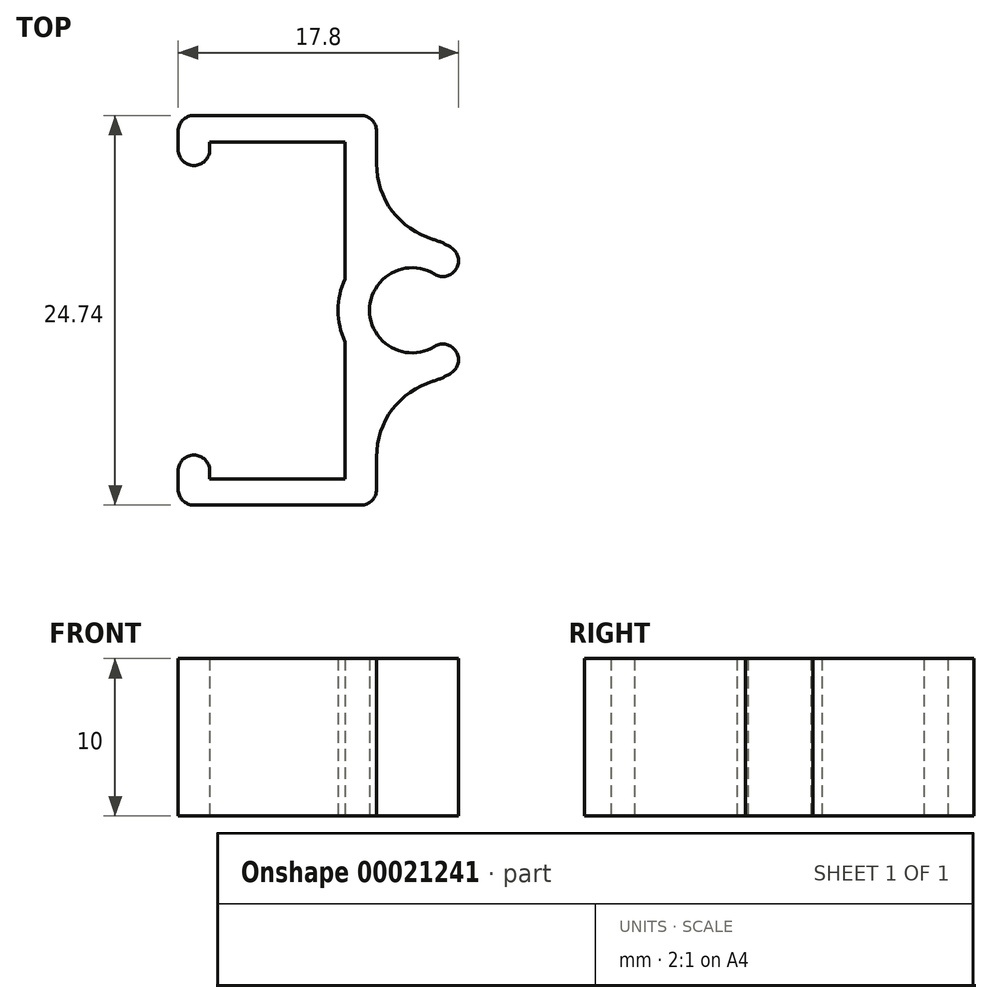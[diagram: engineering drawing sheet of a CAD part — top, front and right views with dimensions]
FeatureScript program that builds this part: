
annotation { "Feature Type Name" : "Feature", "Feature Type Description" : "" }
export const myFeature = defineFeature(function(context is Context, id is Id, definition is map)
    precondition{}
    {
        {
            var Q0;
            Q0=qCreatedBy(makeId("Top.planeOp"),FACE);
            var sketch = newSketch(context, id + "F0", { "sketchPlane" : qUnion([Q0])});
            skLineSegment(sketch, "E0", {"start": v(0.45, 10.7) * mm, "end": v(-8.15, 10.7) * mm});
            skLineSegment(sketch, "E1", {"start": v(-8.15, 10.7) * mm, "end": v(-8.15, 10.2) * mm});
            skLineSegment(sketch, "E2", {"start": v(-9.15, 9.2) * mm, "end": v(-9.15, 9.2) * mm});
            skLineSegment(sketch, "E3", {"start": v(-10.15, 10.2) * mm, "end": v(-10.15, 11.37) * mm});
            skLineSegment(sketch, "E4", {"start": v(-9.15, 12.37) * mm, "end": v(1.45, 12.37) * mm});
            skLineSegment(sketch, "E5.MirrorCS", {"start": v(-8.15, -10.7) * mm, "end": v(-8.15, -10.2) * mm});
            skLineSegment(sketch, "E6.MirrorCS", {"start": v(-9.15, -9.2) * mm, "end": v(-9.15, -9.2) * mm});
            skLineSegment(sketch, "E7.MirrorCS", {"start": v(-10.15, -10.2) * mm, "end": v(-10.15, -11.37) * mm});
            skLineSegment(sketch, "E8.MirrorCS", {"start": v(0.45, -10.7) * mm, "end": v(-8.15, -10.7) * mm});
            skLineSegment(sketch, "E9", {"start": v(2.45, 11.37) * mm, "end": v(2.45, 4.12) * mm});
            skLineSegment(sketch, "E10.MirrorCS", {"start": v(-9.15, -12.37) * mm, "end": v(1.45, -12.37) * mm});
            skLineSegment(sketch, "E11.MirrorCS", {"start": v(2.45, -11.37) * mm, "end": v(2.45, -4.12) * mm});
            skLineSegment(sketch, "E12", {"start": v(0.45, 10.7) * mm, "end": v(0.45, 2) * mm});
            skLineSegment(sketch, "E13.MirrorCS", {"start": v(0.45, -10.7) * mm, "end": v(0.45, -2) * mm});
            skArc(sketch, "E14", {"start": v(7.18, 4) * mm, "mid": v(0, 0) * mm, "end": v(7.18, -4) * mm});
            skPoint(sketch, "E15.visualSharp", {"position": v(2.45, 12.37) * mm});
            skArc(sketch, "E15.filletArc", {"start": v(2.45, 11.37) * mm, "mid": v(2.15, 12.08) * mm, "end": v(1.45, 12.37) * mm});
            skPoint(sketch, "E16.visualSharp", {"position": v(2.45, -12.37) * mm});
            skArc(sketch, "E16.filletArc", {"start": v(1.45, -12.37) * mm, "mid": v(2.15, -12.08) * mm, "end": v(2.45, -11.37) * mm});
            skPoint(sketch, "E17.visualSharp", {"position": v(-10.15, -12.37) * mm});
            skArc(sketch, "E17.filletArc", {"start": v(-10.15, -11.37) * mm, "mid": v(-9.86, -12.08) * mm, "end": v(-9.15, -12.37) * mm});
            skPoint(sketch, "E18.visualSharp", {"position": v(-10.15, -9.2) * mm});
            skArc(sketch, "E18.filletArc", {"start": v(-9.15, -9.2) * mm, "mid": v(-9.86, -9.5) * mm, "end": v(-10.15, -10.2) * mm});
            skPoint(sketch, "E19.visualSharp", {"position": v(-8.15, -9.2) * mm});
            skArc(sketch, "E19.filletArc", {"start": v(-8.15, -10.2) * mm, "mid": v(-8.45, -9.5) * mm, "end": v(-9.15, -9.2) * mm});
            skPoint(sketch, "E20.visualSharp", {"position": v(-8.15, 9.2) * mm});
            skArc(sketch, "E20.filletArc", {"start": v(-9.15, 9.2) * mm, "mid": v(-8.45, 9.5) * mm, "end": v(-8.15, 10.2) * mm});
            skPoint(sketch, "E21.visualSharp", {"position": v(-10.15, 9.2) * mm});
            skArc(sketch, "E21.filletArc", {"start": v(-10.15, 10.2) * mm, "mid": v(-9.86, 9.5) * mm, "end": v(-9.15, 9.2) * mm});
            skPoint(sketch, "E22.visualSharp", {"position": v(-10.15, 12.37) * mm});
            skArc(sketch, "E22.filletArc", {"start": v(-9.15, 12.37) * mm, "mid": v(-9.86, 12.08) * mm, "end": v(-10.15, 11.37) * mm});
            skArc(sketch, "E23.0", {"start": v(6.12, 2.3) * mm, "mid": v(2, 0) * mm, "end": v(6.12, -2.3) * mm});
            skLineSegment(sketch, "E24", {"start": v(7.33, 2.4) * mm, "end": v(7.33, 2.4) * mm});
            skLineSegment(sketch, "E25.MirrorCS", {"start": v(7.33, -2.4) * mm, "end": v(7.33, -2.4) * mm});
            skPoint(sketch, "E26.visualSharp", {"position": v(8.17, 3.18) * mm});
            skArc(sketch, "E26.filletArc", {"start": v(7.33, 2.4) * mm, "mid": v(7.65, 3.24) * mm, "end": v(7.18, 4) * mm});
            skPoint(sketch, "E27.visualSharp", {"position": v(6.7, 1.82) * mm});
            skArc(sketch, "E27.filletArc", {"start": v(6.12, 2.3) * mm, "mid": v(6.74, 2.15) * mm, "end": v(7.33, 2.4) * mm});
            skPoint(sketch, "E28.visualSharp", {"position": v(6.7, -1.82) * mm});
            skArc(sketch, "E28.filletArc", {"start": v(7.33, -2.4) * mm, "mid": v(6.74, -2.15) * mm, "end": v(6.12, -2.3) * mm});
            skPoint(sketch, "E29.visualSharp", {"position": v(8.17, -3.18) * mm});
            skArc(sketch, "E29.filletArc", {"start": v(7.18, -4) * mm, "mid": v(7.65, -3.24) * mm, "end": v(7.33, -2.4) * mm});
            skLineSegment(sketch, "E30", {"start": v(4.7, 0) * mm, "end": v(7.33, 2.4) * mm, "construction": true});
            skLineSegment(sketch, "E31.MirrorCS", {"start": v(4.7, 0) * mm, "end": v(7.33, -2.4) * mm, "construction": true});
            skSolve(sketch);
        }
        {
            var Q0;
            Q0 = qSketchRegion(id + "F0", true);
            var Q1;
            Q1=makeQuery(id+"F0.imprint","IMPRINT",FACE,{"disambiguationData":[TD([[makeQuery(id+"F0.imprint","IMPRINT",EDGE,{"derivedFrom":sQuery(id+"F0.wireOp",EDGE,"E0")}),-1.0]])]});
            extrude(context, id + "F1", {"entities" : qUnion([Q0, Q1]), "depth" : 10 * mm});
        }
        {
            var Q0;
            Q0=makeQuery(id+"F1.opExtrude","SWEPT_EDGE",EDGE,{"disambiguationData":[OSD([sQuery(id+"F0.wireOp",EDGE,"E11.MirrorCS"),sQuery(id+"F0.wireOp",EDGE,"E14")])]});
            var Q1;
            Q1=makeQuery(id+"F1.opExtrude","SWEPT_EDGE",EDGE,{"disambiguationData":[OSD([sQuery(id+"F0.wireOp",EDGE,"E9"),sQuery(id+"F0.wireOp",EDGE,"E14")])]});
            fillet(context, id + "F2", {"entities" : qUnion([Q0, Q1]), "radius" : 5 * mm, "tangentPropagation" : true, "allowEdgeOverflow" : false});
        }
    });
